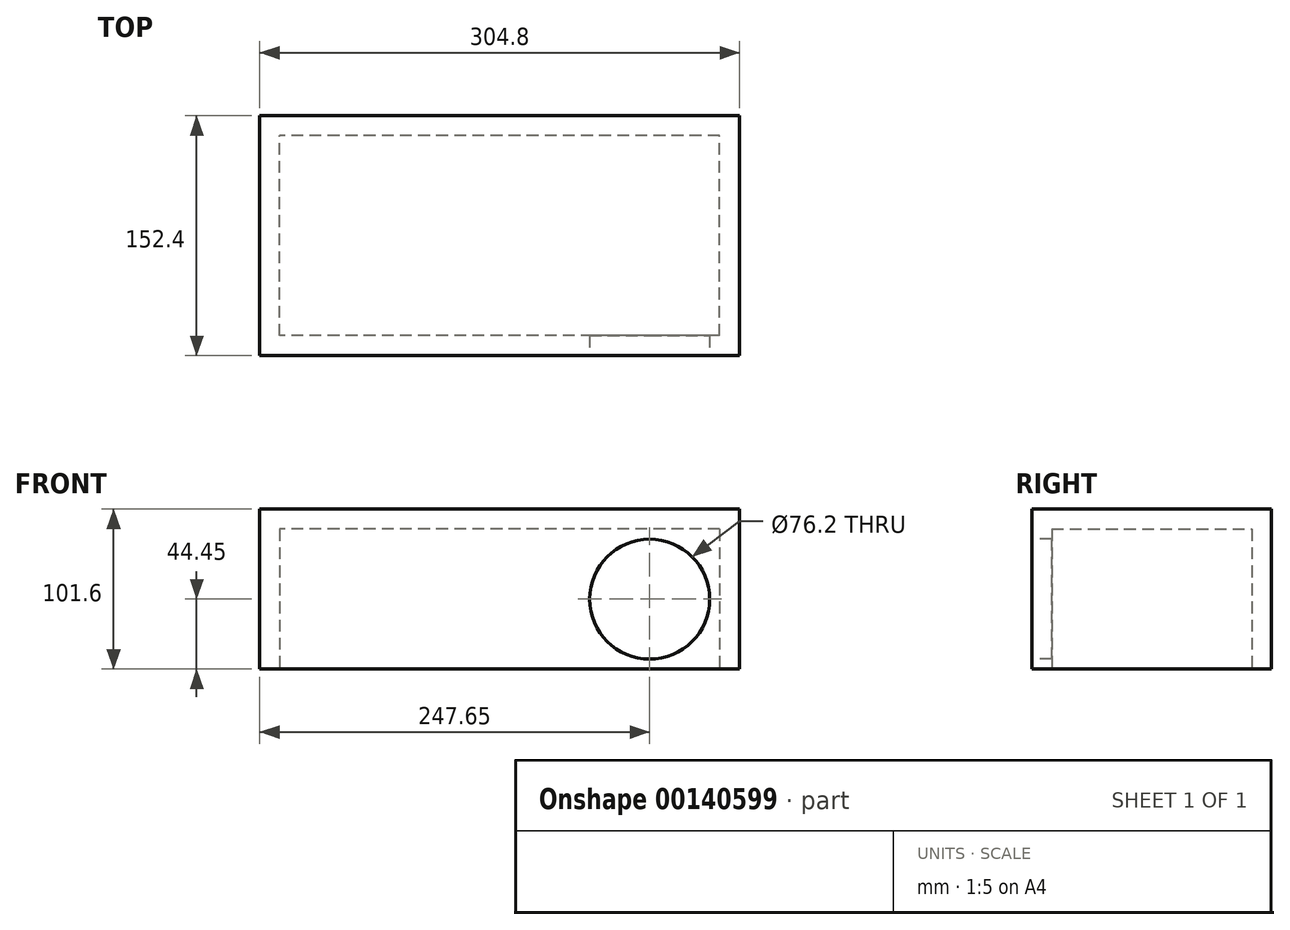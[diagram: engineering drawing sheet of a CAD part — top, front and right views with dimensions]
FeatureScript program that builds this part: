
annotation { "Feature Type Name" : "Feature", "Feature Type Description" : "" }
export const myFeature = defineFeature(function(context is Context, id is Id, definition is map)
    precondition{}
    {
        {
            var Q0;
            Q0=qCreatedBy(makeId("Front.planeOp"),FACE);
            var sketch = newSketch(context, id + "F0", { "sketchPlane" : qUnion([Q0])});
            skLineSegment(sketch, "E0.bottom", {"start": v(152.4, 50.8) * mm, "end": v(-152.4, 50.8) * mm});
            skLineSegment(sketch, "E0.top", {"start": v(152.4, -50.8) * mm, "end": v(-152.4, -50.8) * mm});
            skLineSegment(sketch, "E0.left", {"start": v(152.4, 50.8) * mm, "end": v(152.4, -50.8) * mm});
            skLineSegment(sketch, "E0.right", {"start": v(-152.4, 50.8) * mm, "end": v(-152.4, -50.8) * mm});
            skPoint(sketch, "E0.middle", {"position": v(0, 0) * mm});
            skSolve(sketch);
        }
        {
            var Q0;
            Q0=qSketchRegion(id+"F0",true);
            extrude(context, id + "F1", {"entities" : qUnion([Q0]), "endBound" : BoundingType.SYMMETRIC, "depth" : 152.4 * mm});
        }
        {
            var Q0;
            Q0=makeQuery(id+"F1.opExtrude","SWEPT_FACE",FACE,{"disambiguationData":[OSD([sQuery(id+"F0.wireOp",EDGE,"E0.top")])]});
            var sketch = newSketch(context, id + "F2", { "sketchPlane" : qUnion([Q0])});
            skLineSegment(sketch, "E1.bottom", {"start": v(139.7, 63.5) * mm, "end": v(-139.7, 63.5) * mm});
            skLineSegment(sketch, "E1.top", {"start": v(139.7, -63.5) * mm, "end": v(-139.7, -63.5) * mm});
            skLineSegment(sketch, "E1.left", {"start": v(139.7, 63.5) * mm, "end": v(139.7, -63.5) * mm});
            skLineSegment(sketch, "E1.right", {"start": v(-139.7, 63.5) * mm, "end": v(-139.7, -63.5) * mm});
            skPoint(sketch, "E1.middle", {"position": v(0, 0) * mm});
            skSolve(sketch);
        }
        {
            var Q0;
            Q0=qSketchRegion(id+"F2",true);
            extrude(context, id + "F3", {"entities" : qUnion([Q0]), "operationType" : NewBodyOperationType.REMOVE, "oppositeDirection" : true, "depth" : 88.9 * mm});
        }
        {
            var Q0;
            Q0=makeQuery(id+"F1.opExtrude","CAP_FACE",FACE,{"disambiguationData":[OSD([sQuery(id+"F0.wireOp",EDGE,"E0.bottom"),sQuery(id+"F0.wireOp",EDGE,"E0.top"),sQuery(id+"F0.wireOp",EDGE,"E0.left"),sQuery(id+"F0.wireOp",EDGE,"E0.right")])],"isStart":false});
            var sketch = newSketch(context, id + "F4", { "sketchPlane" : qUnion([Q0])});
            skLineSegment(sketch, "E2", {"start": v(152.4, 0) * mm, "end": v(101.6, 0) * mm, "construction": true});
            skLineSegment(sketch, "E3", {"start": v(101.6, 0) * mm, "end": v(95.25, 0) * mm, "construction": true});
            skLineSegment(sketch, "E4", {"start": v(95.25, 0) * mm, "end": v(95.25, -6.35) * mm, "construction": true});
            skCircle(sketch, "E5", {"center": v(95.25, -6.35) * mm, "radius": 38.1 * mm});
            skSolve(sketch);
        }
        {
            var Q0;
            Q0=qSketchRegion(id+"F4",true);
            extrude(context, id + "F5", {"entities" : qUnion([Q0]), "operationType" : NewBodyOperationType.REMOVE, "oppositeDirection" : true, "depth" : 12.7 * mm});
        }
    });
